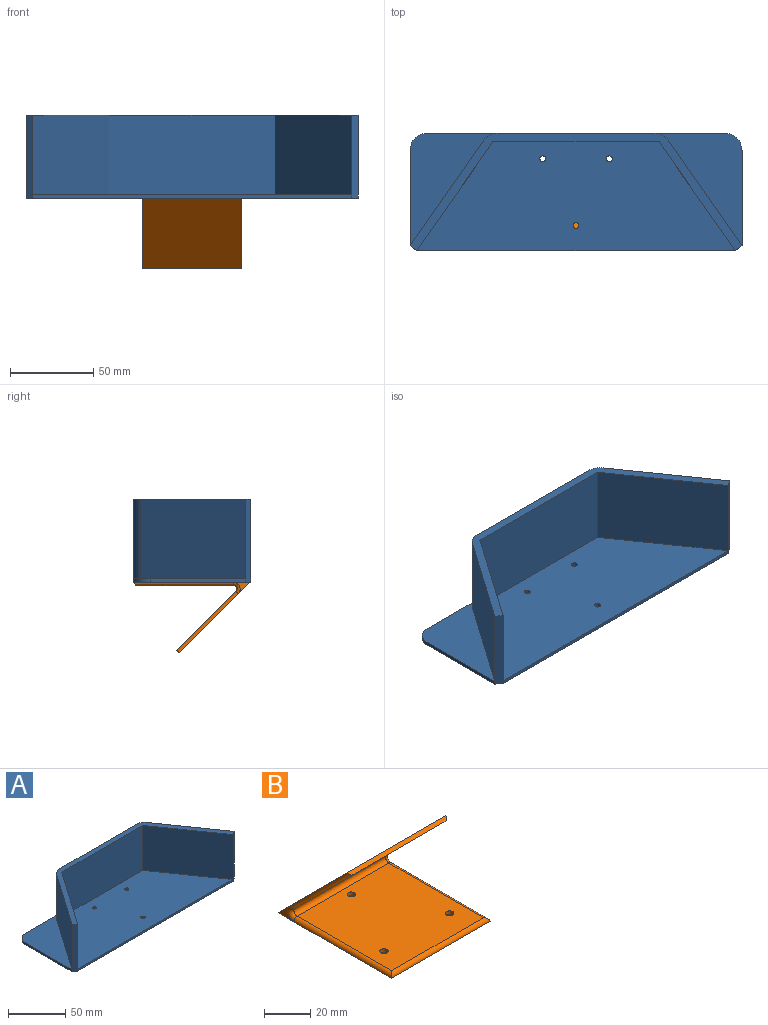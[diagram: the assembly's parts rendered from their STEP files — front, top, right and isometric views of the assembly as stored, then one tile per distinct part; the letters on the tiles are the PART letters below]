
ASSEMBLY  parts=2 mates=1
PART A: 23 faces, bbox 200x70.5x50 mm
  f0: plane 199.96x70.53mm, normal (0,0,-1), area 14018.7mm2, adj f3,f5,f8,f9,f12,f14,f17,f18
  f1: plane 191.77x65.53mm, normal (0,0,1), area 9529.7mm2, adj f2,f6,f8,f13,f20,f21,f22
  f2: plane 100x48mm, normal (0,-1,0), area 4800mm2, adj f1,f6,f7,f13
  f3: plane 179.96x50mm, normal (0,1,0), area 4910.1mm2, adj f0,f7,f10,f15,f16,f17,f18,f19
  f4: plane 63.4x48mm, normal (-0.82,0.57,0), area 3715.1mm2, adj f5,f7,f10,f19
  f5: plane 50x4.1mm, normal (-0.57,-0.82,0), area 250mm2, adj f0,f4,f6,f7,f8,f9
  f6: plane 65.53x48mm, normal (0.82,-0.57,0), area 3840mm2, adj f1,f2,f5,f7
  f7: plane 199.96x70.53mm, normal (0,0,1), area 1317.9mm2, adj f2,f3,f4,f5,f6,f11,f12,f13
  f8: plane 191.77x2mm, normal (0,-1,0), area 383.5mm2, adj f0,f1,f5,f12
  f9: plane 57.66x2mm, normal (-1,0,0), area 115.3mm2, adj f0,f5,f10,f18
  f10: plane 67.66x52.58mm, normal (0,0,1), area 1585.5mm2, adj f3,f4,f9,f18,f19
  f11: plane 63.4x48mm, normal (0.82,0.57,0), area 3715.1mm2, adj f7,f12,f15,f16
  f12: plane 50x4.1mm, normal (0.57,-0.82,0), area 250mm2, adj f0,f7,f8,f11,f13,f14
  f13: plane 65.53x48mm, normal (-0.82,-0.57,0), area 3840mm2, adj f1,f2,f7,f12
  f14: plane 57.66x2mm, normal (1,0,0), area 115.3mm2, adj f0,f12,f15,f17
  f15: plane 67.66x52.58mm, normal (0,0,1), area 1585.5mm2, adj f3,f11,f14,f16,f17
  f16: cylinder r=10mm len=48mm, axis (0,0,-1), area 460.8mm2, adj f3,f7,f11,f15
  f17: cylinder r=10mm len=10mm, axis (0,0,-1), area 31.4mm2, adj f0,f3,f14,f15
  f18: cylinder r=10mm len=10mm, axis (0,0,-1), area 31.4mm2, adj f0,f3,f9,f10
  f19: cylinder r=10mm len=48mm, axis (0,0,-1), area 460.8mm2, adj f3,f4,f7,f10
  f20: cylinder r=1.8mm len=3.6mm, axis (0,0,-1), area 22.6mm2, adj f0,f1
  f21: cylinder r=1.8mm len=3.6mm, axis (0,0,-1), area 22.6mm2, adj f0,f1
  f22: cylinder r=1.8mm len=3.6mm, axis (0,0,-1), area 22.6mm2, adj f0,f1
PART B: 18 faces, bbox 60x69.3x44.3 mm
  f0: plane 69.28x60mm, normal (0,0,-1), area 4126.4mm2, adj f2,f5,f6,f7,f9,f11,f15,f16
  f1: plane 57.63x56mm, normal (0,0,1), area 3196.5mm2, adj f7,f9,f11,f12,f15,f16,f17
  f2: plane 60x42.43mm, normal (0,0.71,0.71), area 3600mm2, adj f0,f3,f5,f6,f8,f14
  f3: plane 60x1.41mm, normal (0,-0.71,0.71), area 118.3mm2, adj f2,f4,f8,f14
  f4: plane 56x35.6mm, normal (0,-0.71,-0.71), area 2819.2mm2, adj f3,f8,f12,f14
  f5: plane 9.66x6.83mm, normal (1,0,0), area 19.8mm2, adj f0,f2,f13
  f6: plane 9.66x6.83mm, normal (-1,0,0), area 19.8mm2, adj f0,f2,f10
  f7: cylinder r=2mm len=59.63mm, axis (0,-1,0), area 185mm2, adj f0,f1,f9,f10
  f8: cylinder r=2mm len=37.01mm, axis (0,0.71,-0.71), area 158.2mm2, adj f2,f3,f4,f10
  f9: cylinder r=2mm len=60mm, axis (-1,0,0), area 183.9mm2, adj f0,f1,f7,f11
  f10: torus R=4mm, axis (1,0,0), area 20.2mm2, adj f6,f7,f8,f12
  f11: cylinder r=2mm len=59.63mm, axis (0,1,0), area 185mm2, adj f0,f1,f9,f13
  f12: cylinder r=2mm len=56mm, axis (-1,0,0), area 263.9mm2, adj f1,f4,f10,f13
  f13: torus R=4mm, axis (1,0,0), area 20.2mm2, adj f5,f11,f12,f14
  f14: cylinder r=2mm len=37.01mm, axis (0,-0.71,0.71), area 158.2mm2, adj f2,f3,f4,f13
  f15: cylinder r=1.8mm len=3.6mm, axis (0,0,-1), area 22.6mm2, adj f0,f1
  f16: cylinder r=1.8mm len=3.6mm, axis (0,0,-1), area 22.6mm2, adj f0,f1
  f17: cylinder r=1.8mm len=3.6mm, axis (0,0,-1), area 22.6mm2, adj f0,f1
PLACE A t=(0,30.35,0)mm
PLACE B rot(axis=(-1,0,0),180deg) t=(-30,-34.55,0)mm
MATE fastened B.f15 <-> A.f22  axis (0,0,1) through (0,-19.91,0)mm
